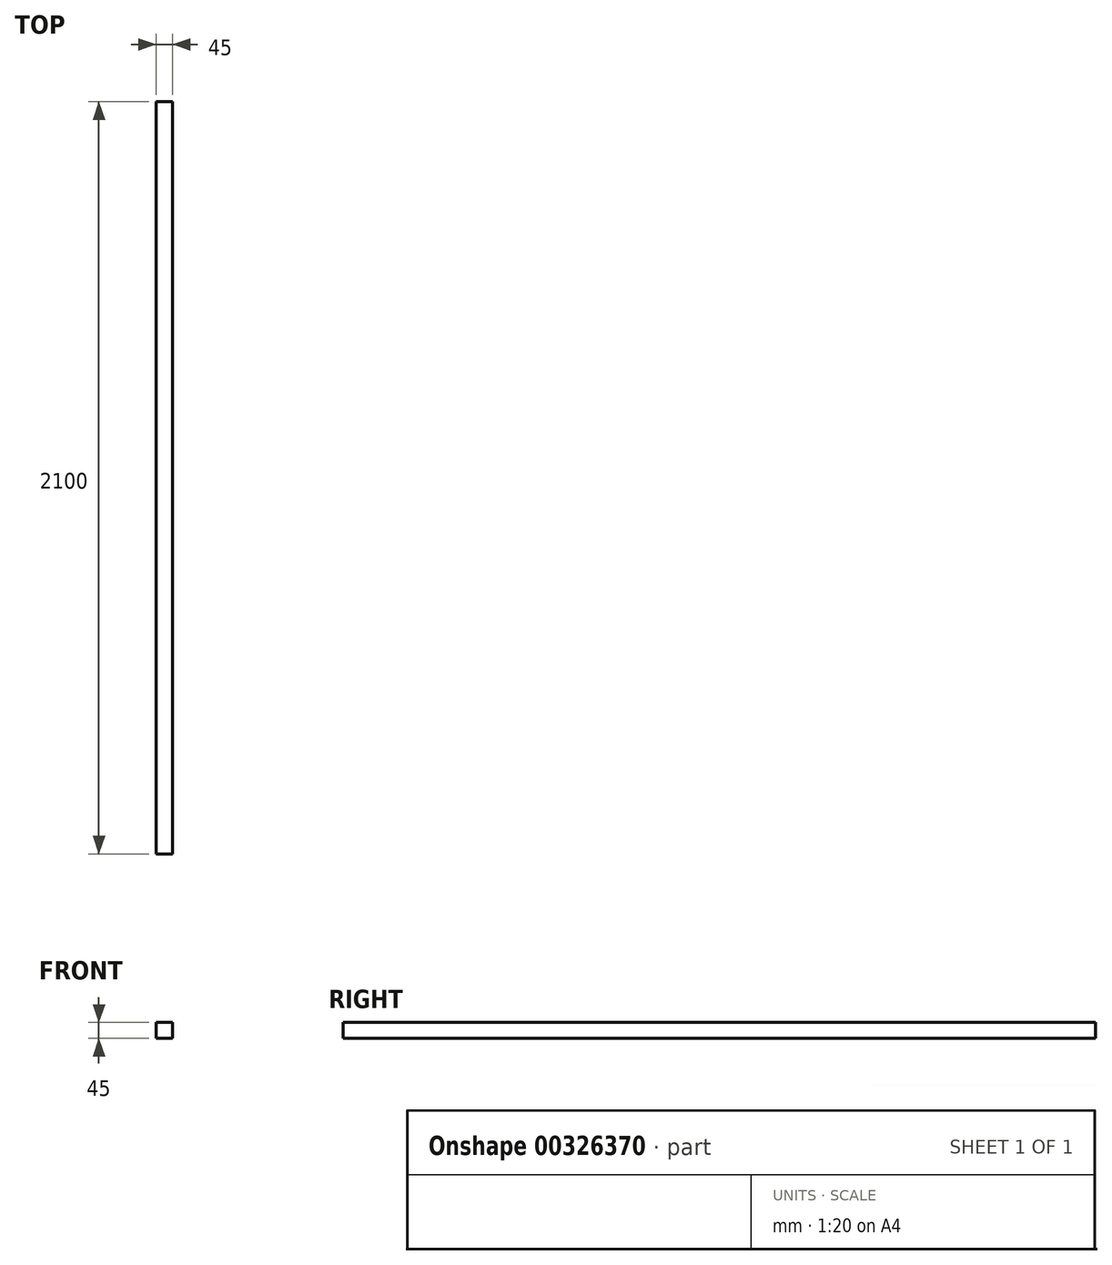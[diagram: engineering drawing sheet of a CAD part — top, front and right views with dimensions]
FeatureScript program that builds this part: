
annotation { "Feature Type Name" : "Feature", "Feature Type Description" : "" }
export const myFeature = defineFeature(function(context is Context, id is Id, definition is map)
    precondition{}
    {
        {
            var Q0;
            Q0=qCreatedBy(makeId("Front.planeOp"),FACE);
            var sketch = newSketch(context, id + "F0", { "sketchPlane" : qUnion([Q0])});
            skLineSegment(sketch, "E0.bottom", {"start": v(0, 0) * mm, "end": v(45, 0) * mm});
            skLineSegment(sketch, "E0.top", {"start": v(0, 45) * mm, "end": v(45, 45) * mm});
            skLineSegment(sketch, "E0.left", {"start": v(0, 0) * mm, "end": v(0, 45) * mm});
            skLineSegment(sketch, "E0.right", {"start": v(45, 0) * mm, "end": v(45, 45) * mm});
            skSolve(sketch);
        }
        {
            var Q0;
            Q0 = qSketchRegion(id + "F0", true);
            extrude(context, id + "F1", {"entities" : qUnion([Q0]), "depth" : 2100 * mm});
        }
    });
